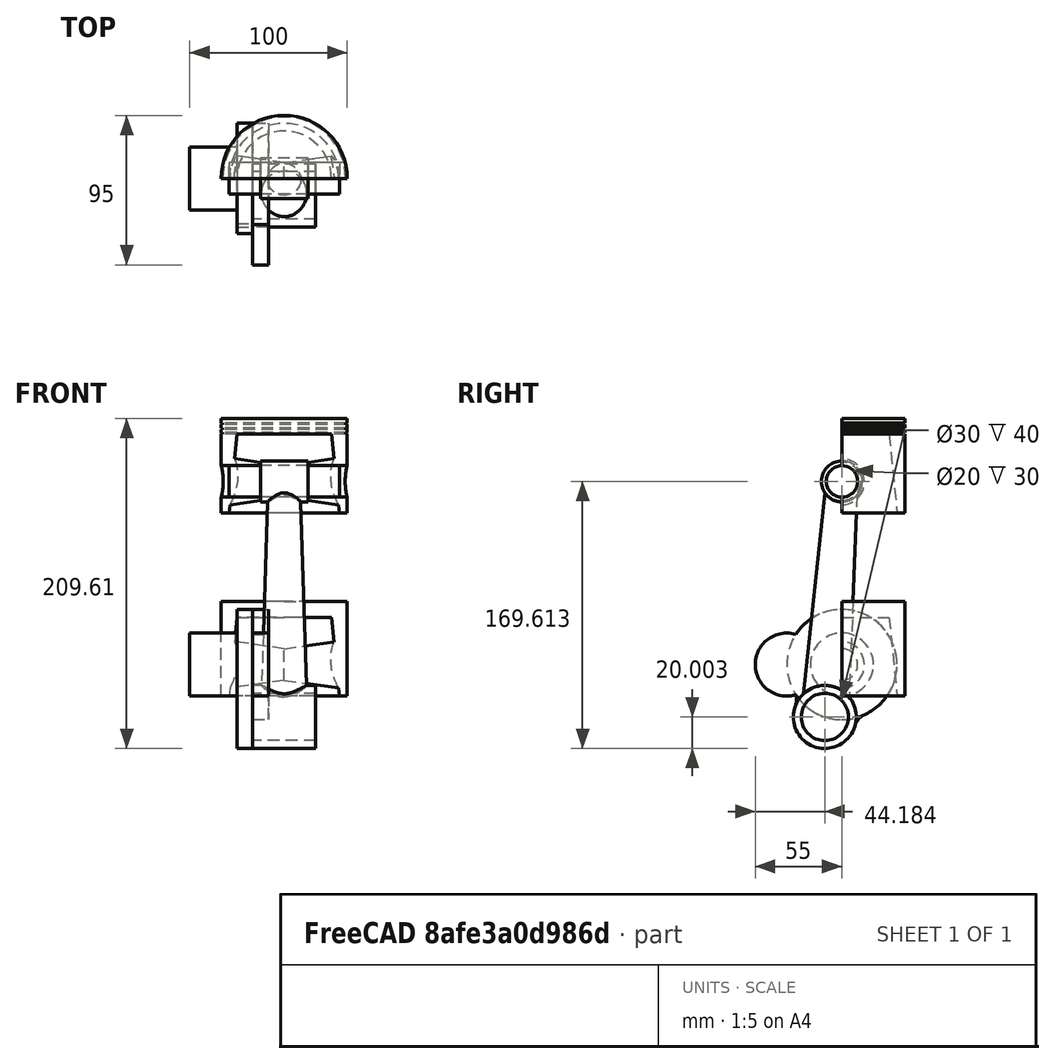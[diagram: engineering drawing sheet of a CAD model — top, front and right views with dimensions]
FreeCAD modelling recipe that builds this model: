
FCSTD DOCUMENT  (FreeCAD 0.18R16093 +53 (Git))
Label: 198 - ENGINE ANIMATION
License: All rights reserved
LicenseURL: http://en.wikipedia.org/wiki/All_rights_reserved
objects: Part::Cylinder×12, Part::Cut×5, Part::Feature×5, Part::MultiFuse×4, App::DocumentObjectGroupPython×4, Part::Cone×3, Part::Compound×3, Part::FeaturePython×1, Part::Fillet×1
note: 34 computed .brp shape members not serialized (recipe doc carries the construction recipe); baked Part::Feature solids carry a one-line shape summary decoded from their .brp

FEATURE [Part::Cylinder] Cylinder
  Angle = 180
  AttacherType = Attacher::AttachEngine3D
  Height = 60
  Placement = pos=(0,0,-20) rot=(0,0,1;0rad)
  Radius = 40
FEATURE [Part::Cone] Cone
  Angle = 360
  AttacherType = Attacher::AttachEngine3D
  Height = 50
  Placement = pos=(0,0,-20) rot=(0,0,1;0rad)
  Radius1 = 35
  Radius2 = 30
FEATURE [Part::Cut] Cut
  Base = -> Cylinder
  Tool = -> Cone
FEATURE [Part::Cone] Cone001
  Angle = 180
  AttacherType = Attacher::AttachEngine3D
  Height = 35
  Placement = pos=(0,0,0) rot=(0,-1,0;1.5708rad)
  Radius1 = 10
  Radius2 = 15
FEATURE [Part::Feature] Cone001001  label="Cone002"
  Placement = pos=(0,0,0) rot=(0,1,0;1.5708rad)
  shape: bbox 35 x 15 x 30 mm, 5 faces (baked)
FEATURE [Part::MultiFuse] Fusion
  Shapes = -> [Cone001001,Cone001,Cut]
FEATURE [Part::Feature] Fusion001
  shape: bbox 80 x 40 x 60 mm, 8 faces (baked)
FEATURE [Part::Cylinder] Cylinder001
  Angle = 360
  AttacherType = Attacher::AttachEngine3D
  Height = 100
  Placement = pos=(50,0,1.1e-14) rot=(0,-1,0;1.5708rad)
  Radius = 10
FEATURE [Part::Cut] Cut001
  Base = -> Fusion001
  Tool = -> Cylinder001
FEATURE [Part::Cylinder] Cylinder002
  Angle = 360
  AttacherType = Attacher::AttachEngine3D
  Height = 30
  Placement = pos=(15,0,3e-15) rot=(0,-1,0;1.5708rad)
  Radius = 13
FEATURE [Part::Cut] Cut002
  Base = -> Cut001
  Tool = -> Cylinder002
FEATURE [Part::FeaturePython] Tube  # WARN: FeaturePython — macro-defined, semantics opaque (R4)
  Height = 1
  InnerRadius = 39
  OuterRadius = 41
  Placement = pos=(0,0,36) rot=(0,0,1;0rad)
FEATURE [Part::Feature] Tube001
  Placement = pos=(0,0,33) rot=(0,0,1;0rad)
  shape: bbox 82 x 82 x 1 mm, 4 faces (baked)
FEATURE [Part::Feature] Tube002
  Placement = pos=(0,0,30) rot=(0,0,1;0rad)
  shape: bbox 82 x 82 x 1 mm, 4 faces (baked)
FEATURE [Part::Compound] Compound
  Links = -> [Tube002,Tube001,Tube]
FEATURE [Part::Cut] Cut003
  Base = -> Cut002
  Tool = -> Compound
FEATURE [Part::Cylinder] Cylinder003
  Angle = 360
  AttacherType = Attacher::AttachEngine3D
  Height = 70
  Placement = pos=(35,0,8e-15) rot=(0,-1,0;1.5708rad)
  Radius = 10
FEATURE [Part::Compound] Compound001  label="PISTON"
  Links = -> [Cylinder003,Cut003]
  Placement = pos=(0,0,116.323) rot=(0,0,1;0rad)
FEATURE [Part::Cylinder] Cylinder004
  Angle = 360
  AttacherType = Attacher::AttachEngine3D
  Height = 30
  Placement = pos=(15,0,150) rot=(0,-1,0;1.5708rad)
  Radius = 13
FEATURE [Part::Cone] Cone001002  label="Cone003"
  Angle = 360
  AttacherType = Attacher::AttachEngine3D
  Height = 150
  Radius1 = 15
  Radius2 = 10
FEATURE [Part::Cylinder] Cylinder005
  Angle = 360
  AttacherType = Attacher::AttachEngine3D
  Height = 40
  Placement = pos=(20,0,4e-15) rot=(0,-1,0;1.5708rad)
  Radius = 20
FEATURE [Part::MultiFuse] Fusion002
  Shapes = -> [Cylinder005,Cone001002,Cylinder004]
FEATURE [Part::Cylinder] Cylinder006
  Angle = 360
  AttacherType = Attacher::AttachEngine3D
  Height = 100
  Placement = pos=(50,0,150) rot=(0,-1,0;1.5708rad)
  Radius = 10
FEATURE [Part::Cylinder] Cylinder007
  Angle = 360
  AttacherType = Attacher::AttachEngine3D
  Height = 100
  Placement = pos=(50,0,1.1e-14) rot=(0,-1,0;1.5708rad)
  Radius = 15
FEATURE [Part::Compound] Compound002
  Links = -> [Cylinder007,Cylinder006]
FEATURE [Part::Cut] Cut004  label="CRANK"
  Base = -> Fusion002
  Placement = pos=(0,-10.8156,-33.287) rot=(1,0,0;6.21102rad)
  Tool = -> Compound002
FEATURE [Part::Cylinder] Cylinder008
  Angle = 360
  AttacherType = Attacher::AttachEngine3D
  Height = 10
  Placement = pos=(-20,-35,-4e-15) rot=(0,1,0;1.5708rad)
  Radius = 20
FEATURE [Part::Cylinder] Cylinder009
  Angle = 360
  AttacherType = Attacher::AttachEngine3D
  Height = 10
  Placement = pos=(-20,0,-4e-15) rot=(0,1,0;1.5708rad)
  Radius = 35
FEATURE [Part::MultiFuse] Fusion003
  Shapes = -> [Cylinder009,Cylinder008]
FEATURE [Part::Feature] Fusion003001  label="Fusion004"
  shape: bbox 10 x 90 x 70 mm, 4 faces (baked)
FEATURE [Part::Fillet] Fillet
  Base = -> Fusion003001
  Edges = 2 edges r=10: [Edge5,Edge8]
  Placement = pos=(-10,0,0) rot=(0,0,1;0rad)
FEATURE [Part::Cylinder] Cylinder010
  Angle = 360
  AttacherType = Attacher::AttachEngine3D
  Height = 40
  Placement = pos=(-20,-35,-4e-15) rot=(0,1,0;1.5708rad)
  Radius = 15
FEATURE [Part::Cylinder] Cylinder011
  Angle = 360
  AttacherType = Attacher::AttachEngine3D
  Height = 30
  Placement = pos=(-30,0,-7e-15) rot=(0,-1,0;1.5708rad)
  Radius = 20
FEATURE [Part::MultiFuse] Fusion003002  label="CRANKSHAFT"
  Placement = pos=(0,0,0) rot=(1,0,0;1.25664rad)
  Shapes = -> [Cylinder011,Cylinder010,Fillet]
FEATURE [App::DocumentObjectGroupPython] My_Placer  # scripted group (container) (typed FeaturePython)
  Placement = pos=(0,0,0) rot=(1,0,0;-5.02655rad)
  RotAxis = (1,0,0)
  RotCenter = (0,0,0)
  arc = -time*360
  arc0 = 0
  arc1 = 90
  target = -> Fusion003002
  time = 0.8
  x = 0
  x0 = 0
  x1 = 200
  y = 0
  y0 = 0
  y1 = 0
  z = 0
  z0 = 0
  z1 = 0
FEATURE [App::DocumentObjectGroupPython] My_Placer001  # scripted group (container) (typed FeaturePython)
  Placement = pos=(0,0,116.323) rot=(0,0,1;0rad)
  RotAxis = (0,0,1)
  RotCenter = (0,0,0)
  arc = 0
  arc0 = 0
  arc1 = 90
  target = -> Compound001
  time = 0.8
  x = 0
  x0 = 0.309017
  x1 = -0.951057
  y = 0
  y0 = 0.072104
  y1 = 0.0721666
  z = 150*z1+35*x1
  z0 = 4.13484
  z1 = 0.997397
  expr: z1 = cos(z0)
  expr: z0 = y1 * 180 / pi
  expr: y1 = y0 + 1 / 2 * y0 ^ 3 / 3 + 3 / 8 * y0 ^ 5 / 5 + 15 / 48 * y0 ^ 7 / 7
  expr: y0 = x0 * 35 / 150
  expr: x1 = sin(time * 360)
  expr: x0 = cos(time * 360)
FEATURE [App::DocumentObjectGroupPython] My_Placer002  # scripted group (container) (typed FeaturePython)
  Placement = pos=(0,-10.8156,-33.287) rot=(1,0,0;-0.072167rad)
  RotAxis = (1,0,0)
  RotCenter = (0,0,0)
  arc =  -z0
  arc0 = 0
  arc1 = 90
  target = -> Cut004
  time = 0.8
  x = 0
  x0 = 0.309017
  x1 = -0.951057
  y = -35*x0
  y0 = 0.072104
  y1 = 0.0721666
  z = 35*x1
  z0 = 4.13484
  z1 = 0.997397
  expr: z1 = cos(z0)
  expr: z0 = y1 * 180 / pi
  expr: y1 = y0 + 1 / 2 * y0 ^ 3 / 3 + 3 / 8 * y0 ^ 5 / 5 + 15 / 48 * y0 ^ 7 / 7
  expr: y0 = x0 * 35 / 150
  expr: x1 = sin(time * 360)
  expr: x0 = cos(time * 360)
FEATURE [App::DocumentObjectGroupPython] My_Manager  # scripted group (container) (typed FeaturePython)
  Group = -> [My_Placer,My_Placer001,My_Placer002]
  intervall = 1000
  sleeptime = 0.02
  start = 0
  step = 80
  text = NO
